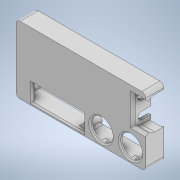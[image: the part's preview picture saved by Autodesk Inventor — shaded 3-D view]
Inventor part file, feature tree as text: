
AUTODESK INVENTOR PART (.ipt)
format: ipt  version: 2021 (Build 250183000, 183)  size: 558,080 bytes
history: native  units: mm
features: sketch x26, extrude x23, chamfer x8, fillet x6, hole x3
ambient origin geometry x8: Origin, YZ Plane, XZ Plane, XY Plane, X Axis, Y Axis, Z Axis, Center Point
bodies: Solid1 (feature_tree)
feature tree (66):
  extrude  "Extrusion1"  Depth=52.0mm
  extrude  "Extrusion2"  Depth=50.0mm
  extrude  "Extrusion3"  Depth=2.0mm
  extrude  "Extrusion4"  Depth=2.0mm
  fillet  "Fillet1"  Radius=2.0mm
  chamfer  "Chamfer1"  Distance=12.0mm
  extrude  "Extrusion5"  Depth=10.4mm
  extrude  "Extrusion6"  Depth=10.4mm
  extrude  "Extrusion7"  Depth=17.0mm
  extrude  "Extrusion8"  Depth=2.0mm
  extrude  "Extrusion9"  Depth=2.0mm
  chamfer  "Chamfer2"  Distance=2.0mm
  extrude  "Extrusion10"  Depth=1.0mm TaperAngle=45.0deg
  fillet  "Fillet3"  Radius=88.0mm
  chamfer  "Chamfer3"  Distance=20.0mm
  extrude  "Extrusion11"  Depth=2.0mm TaperAngle=0.0deg
  extrude  "Extrusion12"  Depth=11.0mm
  hole  "Hole1"  [1 undecoded]
  extrude  "Extrusion13"  TaperAngle=0.0deg  [1 undecoded]
  hole  "Hole2"  [1 undecoded]
  extrude  "Extrusion14"  Depth=12.0mm
  extrude  "Extrusion15"  Depth=2.0mm TaperAngle=45.0deg
  extrude  "Extrusion16"  Depth=40.0mm
  extrude  "Extrusion17"  Depth=3.5mm
  fillet  "Fillet4"  Radius=14.0mm
  extrude  "Extrusion21"  Depth=2.0mm TaperAngle=0.0deg
  chamfer  "Chamfer6"  Distance=1.0mm Angle=45.0deg
  extrude  "Extrusion22"  Depth=49.0mm
  extrude  "Extrusion23"  Depth=2.0mm
  extrude  "Extrusion24"  Depth=2.0mm
  chamfer  "Chamfer8"  Distance=49.0mm
  chamfer  "Chamfer9"  Distance=2.0mm
  fillet  "Fillet5"  Radius=2.0mm
  extrude  "Extrusion25"  Depth=2.0mm
  fillet  "Fillet6"  Radius=5.0mm
  chamfer  "Chamfer11"  Distance=5.0mm
  extrude  "Extrusion26"  Depth=2.0mm
  hole  "Hole3"  [1 undecoded]
  chamfer  "Chamfer12"  Distance=3.0mm
  fillet  "Fillet7"  Radius=3.0mm
  sketch  "Sketch1"  dims[d0=100.0mm d1=52.0mm]
  sketch  "Sketch2"  dims[d2=26.0mm d3=50.0mm]
  sketch  "Sketch3"  dims[d4=2.0mm d5=0.0mm d6=2.0mm]
  sketch  "Sketch4"  dims[d7=2.0mm d8=2.0mm d9=2.0mm d10=12.0mm d11=0.0mm]
  sketch  "Sketch5"  dims[d12=65.5mm d13=10.4mm]
  sketch  "Sketch6"  dims[d14=88.25mm d15=10.4mm]
  sketch  "Sketch7"  dims[d16=17.0mm d17=17.0mm]
  sketch  "Sketch8"  dims[d18=2.0mm d19=0.0mm d20=40.0mm]
  sketch  "Sketch9"  dims[d21=13.0mm d22=2.0mm]
  sketch  "Sketch10"  dims[d23=12.0mm d24=2.0mm d25=0.0mm]
  sketch  "Sketch11"  dims[d26=3.0mm d27=1.0mm d28=2.0mm d29=45.0deg d30=88.0mm]
  sketch  "Sketch12"  dims[d31=29.0mm]
  sketch  "Sketch13"  dims[d32=23.0mm d33=20.0mm d34=0.0mm]
  sketch  "Sketch14"  dims[d35=2.0mm d36=0.0mm d37=2.0mm d38=0.0mm]
  sketch  "Sketch15"  dims[d39=11.0mm d40=11.0mm]
  sketch  "Sketch16"  dims[d41=42.0mm d42=29.0mm]
  sketch  "Sketch17"  dims[d43=7.0mm d44=0.0mm]
  sketch  "Sketch18"  dims[d45=5.8mm d46=5.8mm]
  sketch  "Sketch19"  dims[d47=2.0mm d48=0.0mm d49=12.0mm]
  sketch  "Sketch23"  dims[d50=20.0mm d51=0.0mm d52=2.0mm d53=2.0mm d54=45.0deg]
  sketch  "Sketch24"  dims[d56=30.0mm d57=40.0mm]
  sketch  "Sketch25"  dims[d58=3.5mm d59=6.0mm d60=14.0mm]
  sketch  "Sketch27"  dims[d61=16.0mm d62=2.0mm d63=0.0mm]
  sketch  "Sketch28"  dims[d64=1.0mm d65=1.0mm d66=2.0mm d67=45.0deg]
  sketch  "Sketch29"  dims[d68=3.0mm d69=49.0mm]
  sketch  "Sketch30"  dims[d70=60.0mm d71=49.0mm d72=85.0mm d73=49.0mm d74=2.0mm d75=2.0mm d76=2.0mm d77=5.0mm d78=5.0mm d79=5.0mm d80=12.0mm d81=0.0mm d82=3.0mm d83=3.0mm d84=2.0mm d85=5.0mm d86=12.0mm d87=0.0mm d88=2.0mm d89=6.0mm d90=4.0mm d91=2.0mm d92=90.0deg d93=6.5mm d94=20.594885mm d95=8.0mm d96=97.0mm d97=4.2mm d98=12.0mm d99=0.0mm d100=2.0mm d101=6.0mm d102=4.0mm d103=2.0mm d104=90.0deg d105=6.5mm d106=20.594885mm d107=7.0mm d108=5.8mm d109=5.8mm d110=2.0mm d111=11.0mm d112=0.0mm d113=1.0mm d114=0.0mm d115=2.0mm d116=10.0mm d117=0.0mm d118=0.0mm d119=1.0mm d120=0.0mm d160=2.0mm d161=5.0mm d162=1.0mm d163=1.0mm d164=11.0mm d165=0.0mm d166=4.0mm d167=2.0mm d168=45.0deg d169=7.0mm d170=14.0mm d171=0.0mm d172=12.0mm d173=10.0mm d174=0.0mm d182=4.0mm d183=0.0mm d184=0.0mm d185=10.0mm d186=0.0mm d187=2.0mm d188=2.0mm d189=45.0deg d190=2.0mm d191=2.0mm d192=45.0deg d193=3.0mm d194=17.0mm d195=17.0mm d196=5.0mm d197=0.0mm d201=2.0mm d202=1.5mm d203=2.0mm d204=45.0deg d205=50.0mm d206=3.0mm d207=5.0mm d208=7.5mm d209=0.0mm d210=2.0mm d211=6.0mm d212=4.0mm d213=2.0mm d214=90.0deg d215=6.5mm d216=20.594885mm d217=3.49mm d218=2.0mm d219=45.0deg d220=2.0mm d221=0.375mm]
note: 4 required parameter values undecoded (feature->parameter linkage not recoverable at this tier; creation-order binding heuristic only, values carry confidence <= 0.55)
